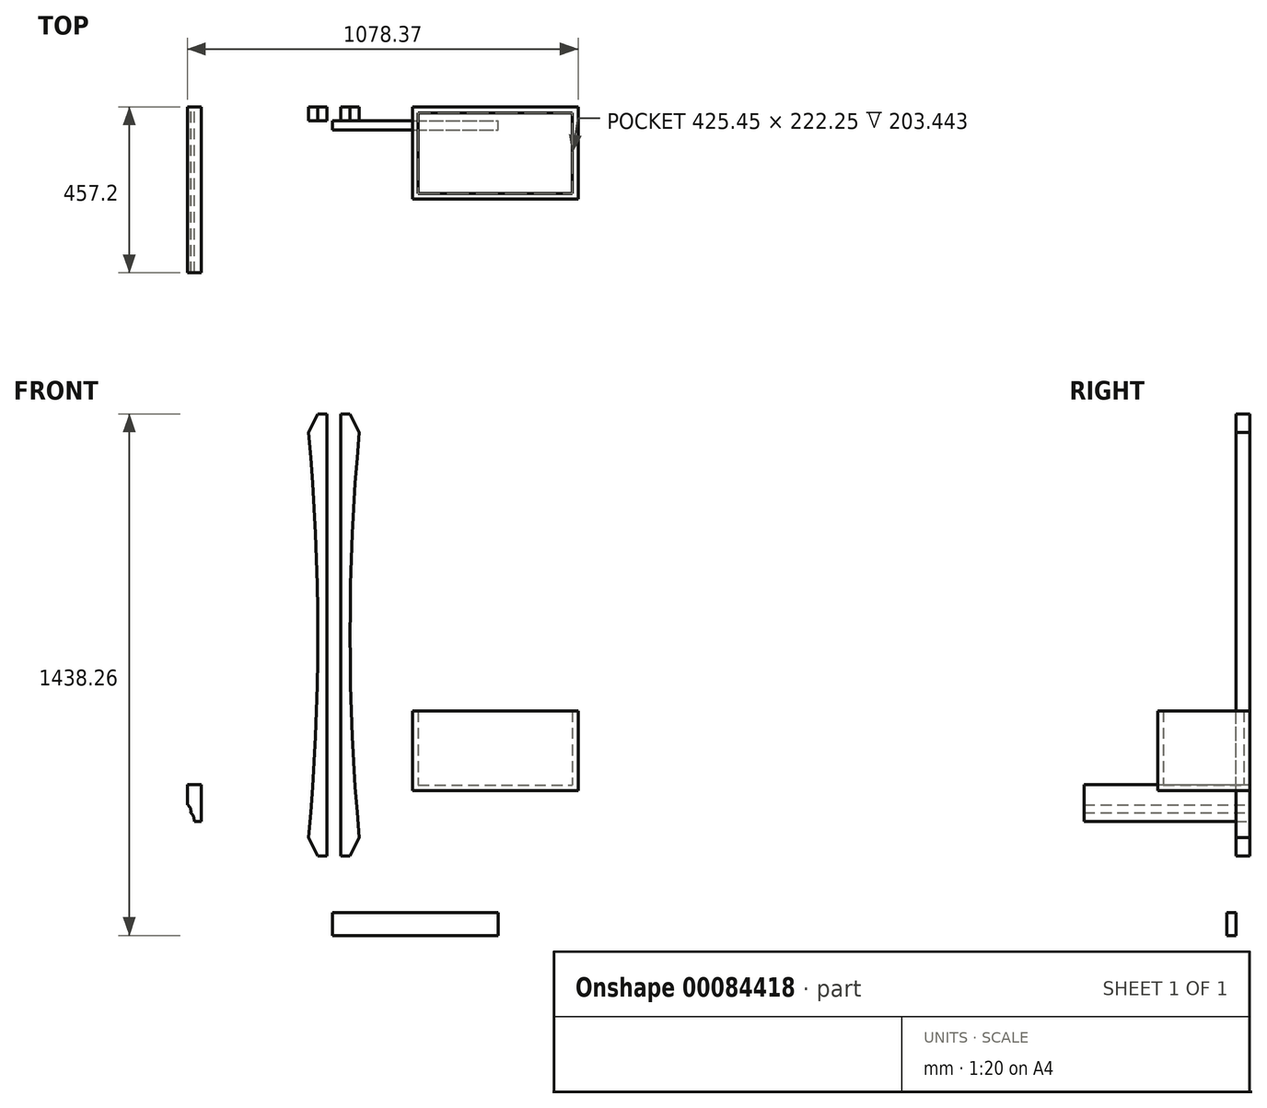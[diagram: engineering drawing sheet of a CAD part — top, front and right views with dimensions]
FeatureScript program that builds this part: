
annotation { "Feature Type Name" : "Feature", "Feature Type Description" : "" }
export const myFeature = defineFeature(function(context is Context, id is Id, definition is map)
    precondition{}
    {
        {
            var Q0;
            Q0=qCreatedBy(makeId("Front.planeOp"),FACE);
            var sketch = newSketch(context, id + "F0", { "sketchPlane" : qUnion([Q0])});
            skLineSegment(sketch, "E0.bottom", {"start": v(-44.54, 1124.41) * mm, "end": v(-19.14, 1124.41) * mm});
            skLineSegment(sketch, "E0.top", {"start": v(-44.54, -94.79) * mm, "end": v(-19.14, -94.79) * mm});
            skLineSegment(sketch, "E0.right", {"start": v(-19.14, 1124.41) * mm, "end": v(-19.14, -94.79) * mm});
            skFitSpline(sketch, "E1", {"points": [v(-44.54, -94.79) * mm, v(-69.94, -43.99) * mm], "startDerivative": vector(-25.4, 50.8) * mm, "endDerivative": vector(-25.4, 50.8) * mm});
            skArc(sketch, "E2", {"start": v(-69.94, -43.99) * mm, "mid": v(-44.54, 514.81) * mm, "end": v(-69.94, 1073.61) * mm});
            skLineSegment(sketch, "E3", {"start": v(-69.94, 1073.61) * mm, "end": v(-44.54, 1124.41) * mm});
            skPoint(sketch, "E4.orphan", {"position": v(-69.94, 1124.41) * mm});
            skPoint(sketch, "E5.orphan", {"position": v(-69.94, 514.81) * mm});
            skPoint(sketch, "E6.end.orphan", {"position": v(-19.14, 514.81) * mm});
            skPoint(sketch, "E7.start.orphan", {"position": v(-44.54, 514.81) * mm});
            skPoint(sketch, "E8.orphan", {"position": v(-69.94, -94.79) * mm});
            skPoint(sketch, "E9.end.orphan", {"position": v(-19.14, -43.99) * mm});
            skSolve(sketch);
        }
        {
            var Q0;
            Q0=makeQuery(id+"F0.imprint","IMPRINT",FACE,{"disambiguationData":[TD([[makeQuery(id+"F0.imprint","IMPRINT",EDGE,{"derivedFrom":sQuery(id+"F0.wireOp",EDGE,"E0.bottom")}),-1.0]])]});
            extrude(context, id + "F1", {"entities" : qUnion([Q0]), "depth" : 38.1 * mm});
        }
        {
            var Q0;
            Q0=makeQuery(id+"F1.opExtrude","SWEPT_BODY",BODY,{"disambiguationData":[OSD([sQuery(id+"F0.wireOp",EDGE,"E0.bottom"),sQuery(id+"F0.wireOp",EDGE,"E0.top"),sQuery(id+"F0.wireOp",EDGE,"E0.right"),sQuery(id+"F0.wireOp",EDGE,"E1"),sQuery(id+"F0.wireOp",EDGE,"E2"),sQuery(id+"F0.wireOp",EDGE,"E3")])]});
            var Q1;
            Q1=qCreatedBy(makeId("Right.planeOp"),FACE);
            mirror(context, id + "F2", {"entities" : qUnion([Q0]), "mirrorPlane" : qUnion([Q1])});
        }
        {
            var Q0;
            Q0=makeQuery(id+"F2.opPattern","COPY",FACE,{"derivedFrom":makeQuery(id+"F1.opExtrude","CAP_FACE",FACE,{"disambiguationData":[OSD([sQuery(id+"F0.wireOp",EDGE,"E0.bottom"),sQuery(id+"F0.wireOp",EDGE,"E0.top"),sQuery(id+"F0.wireOp",EDGE,"E0.right"),sQuery(id+"F0.wireOp",EDGE,"E1"),sQuery(id+"F0.wireOp",EDGE,"E2"),sQuery(id+"F0.wireOp",EDGE,"E3")])],"isStart":false}),"instanceName":"1"});
            var sketch = newSketch(context, id + "F3", { "sketchPlane" : qUnion([Q0])});
            skLineSegment(sketch, "E10.bottom", {"start": v(-3.61, -250.35) * mm, "end": v(453.59, -250.35) * mm});
            skLineSegment(sketch, "E10.top", {"start": v(-3.61, -313.85) * mm, "end": v(453.59, -313.85) * mm});
            skLineSegment(sketch, "E10.left", {"start": v(-3.61, -250.35) * mm, "end": v(-3.61, -313.85) * mm});
            skLineSegment(sketch, "E10.right", {"start": v(453.59, -250.35) * mm, "end": v(453.59, -313.85) * mm});
            skSolve(sketch);
        }
        {
            var Q0;
            Q0=makeQuery(id+"F3.imprint","IMPRINT",FACE,{"disambiguationData":[TD([[makeQuery(id+"F3.imprint","IMPRINT",EDGE,{"derivedFrom":sQuery(id+"F3.wireOp",EDGE,"E10.bottom")}),-1.0]])]});
            extrude(context, id + "F4", {"entities" : qUnion([Q0]), "depth" : 25.4 * mm});
        }
        {
            var Q0;
            Q0=qCreatedBy(makeId("Front.planeOp"),FACE);
            var sketch = newSketch(context, id + "F5", { "sketchPlane" : qUnion([Q0])});
            skLineSegment(sketch, "E11.bottom", {"start": v(-404.64, 101.6) * mm, "end": v(-366.54, 101.6) * mm});
            skLineSegment(sketch, "E11.top", {"start": v(-385.6, 0) * mm, "end": v(-366.54, 0) * mm});
            skLineSegment(sketch, "E11.left", {"start": v(-404.64, 101.6) * mm, "end": v(-404.64, 46.6) * mm});
            skLineSegment(sketch, "E11.right", {"start": v(-366.54, 101.6) * mm, "end": v(-366.54, 0) * mm});
            skArc(sketch, "E12", {"start": v(-385.6, 0) * mm, "mid": v(-387.26, 13.56) * mm, "end": v(-394.82, 24.95) * mm});
            skArc(sketch, "E13", {"start": v(-394.82, 24.95) * mm, "mid": v(-396.27, 37.35) * mm, "end": v(-404.64, 46.6) * mm});
            skPoint(sketch, "E14.orphan", {"position": v(-404.64, 0) * mm});
            skSolve(sketch);
        }
        {
            var Q0;
            Q0 = qSketchRegion(id + "F5", true);
            extrude(context, id + "F6", {"entities" : qUnion([Q0]), "depth" : 457.2 * mm});
        }
        {
            var Q0;
            Q0=qCreatedBy(makeId("Front.planeOp"),FACE);
            var sketch = newSketch(context, id + "F7", { "sketchPlane" : qUnion([Q0])});
            skLineSegment(sketch, "E15.bottom", {"start": v(216.53, 304.8) * mm, "end": v(673.73, 304.8) * mm});
            skLineSegment(sketch, "E15.top", {"start": v(216.53, 85.47) * mm, "end": v(673.73, 85.47) * mm});
            skLineSegment(sketch, "E15.left", {"start": v(216.53, 304.8) * mm, "end": v(216.53, 85.47) * mm});
            skLineSegment(sketch, "E15.right", {"start": v(673.73, 304.8) * mm, "end": v(673.73, 85.47) * mm});
            skSolve(sketch);
        }
        {
            var Q0;
            Q0=makeQuery(id+"F7.imprint","IMPRINT",FACE,{"disambiguationData":[TD([[makeQuery(id+"F7.imprint","IMPRINT",EDGE,{"derivedFrom":sQuery(id+"F7.wireOp",EDGE,"E15.bottom")}),-1.0]])]});
            extrude(context, id + "F8", {"entities" : qUnion([Q0]), "operationType" : NewBodyOperationType.ADD, "depth" : 254 * mm});
        }
        {
            var Q0;
            Q0=makeQuery(id+"F8.opExtrude","SWEPT_FACE",FACE,{"disambiguationData":[OSD([sQuery(id+"F7.wireOp",EDGE,"E15.bottom")])]});
            shell(context, id + "F9", {"entities" : qUnion([Q0]), "thickness" : 15.88 * mm});
        }
    });
